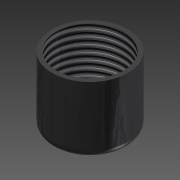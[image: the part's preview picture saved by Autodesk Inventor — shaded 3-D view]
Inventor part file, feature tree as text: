
AUTODESK INVENTOR PART (.ipt)
format: ipt  version: 2015 (Build 190159000, 159)  size: 126,464 bytes
history: native  units: mm
features: other x1, extrude x1, shell x1, thread x1, fillet x1, sketch x1
ambient origin geometry x8: Origin, YZ Plane, XZ Plane, XY Plane, X Axis, Y Axis, Z Axis, Center Point
bodies: Body1 (feature_tree)
feature tree (6):
  other  "Bryła1"
  extrude  "Wyciągnięcie proste1"  Depth=9.0mm
  shell  "Skorupa1"  Thickness=8.0mm
  thread  "Gwint1"
  fillet  "Zaokrąglenie1"  Radius=0.5mm
  sketch  "Szkic1"
